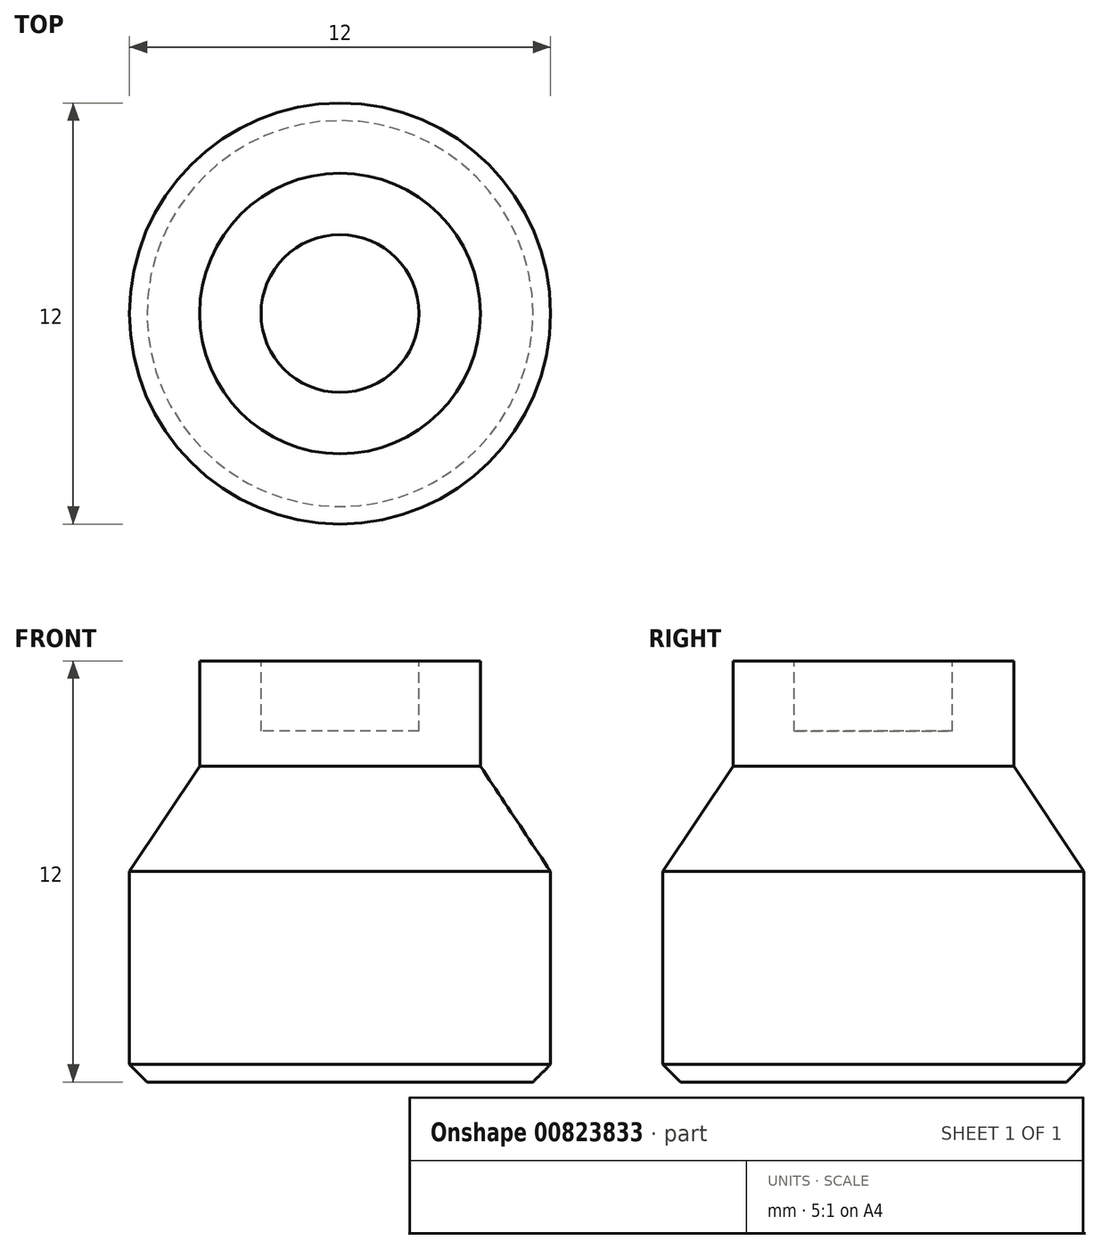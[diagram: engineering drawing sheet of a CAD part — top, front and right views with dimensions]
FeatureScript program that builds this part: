
annotation { "Feature Type Name" : "Feature", "Feature Type Description" : "" }
export const myFeature = defineFeature(function(context is Context, id is Id, definition is map)
    precondition{}
    {
        {
            var Q0;
            Q0=qCreatedBy(makeId("Front.planeOp"),FACE);
            var sketch = newSketch(context, id + "F0", { "sketchPlane" : qUnion([Q0])});
            skLineSegment(sketch, "E0", {"start": v(0, 0) * mm, "end": v(6, 0) * mm});
            skLineSegment(sketch, "E1", {"start": v(6, 0) * mm, "end": v(6, 6) * mm});
            skLineSegment(sketch, "E2", {"start": v(6, 6) * mm, "end": v(4, 9) * mm});
            skLineSegment(sketch, "E3", {"start": v(4, 9) * mm, "end": v(4, 12) * mm});
            skLineSegment(sketch, "E4", {"start": v(4, 12) * mm, "end": v(0, 12) * mm});
            skLineSegment(sketch, "E5", {"start": v(0, 12) * mm, "end": v(0, 0) * mm});
            skSolve(sketch);
        }
        {
            var Q0;
            Q0=makeQuery(id+"F0.imprint","IMPRINT",FACE,{"disambiguationData":[TD([[makeQuery(id+"F0.imprint","IMPRINT",EDGE,{"derivedFrom":sQuery(id+"F0.wireOp",EDGE,"E0")}),1.0]])]});
            var Q1;
            Q1=sQuery(id+"F0.wireOp",EDGE,"E5");
            revolve(context, id + "F1", {"surfaceOperationType" : NewSurfaceOperationType.NEW, "entities" : qUnion([Q0]), "axis" : qUnion([Q1]), "revolveType" : RevolveType.FULL});
        }
        {
            var Q0;
            Q0=makeQuery(id+"F1.opRevolve","SWEPT_FACE",FACE,{"disambiguationData":[OSD([sQuery(id+"F0.wireOp",EDGE,"E4")])]});
            var sketch = newSketch(context, id + "F2", { "sketchPlane" : qUnion([Q0])});
            skCircle(sketch, "E6", {"center": v(0, 0) * mm, "radius": 2.25 * mm});
            skSolve(sketch);
        }
        {
            var Q0;
            Q0=makeQuery(id+"F2.imprint","IMPRINT",FACE,{"disambiguationData":[TD([[makeQuery(id+"F2.imprint","IMPRINT",EDGE,{"derivedFrom":sQuery(id+"F2.wireOp",EDGE,"E6")}),1.0]])]});
            extrude(context, id + "F3", {"entities" : qUnion([Q0]), "operationType" : NewBodyOperationType.REMOVE, "oppositeDirection" : true, "depth" : 2 * mm, "offsetDistance" : 25 * mm});
        }
        {
            var Q0;
            Q0=makeQuery(id+"F1.opRevolve","SWEPT_EDGE",EDGE,{"disambiguationData":[OSD([sQuery(id+"F0.wireOp",EDGE,"E0"),sQuery(id+"F0.wireOp",EDGE,"E1")])]});
            chamfer(context, id + "F4", {"entities" : qUnion([Q0]), "width" : .5 * mm, "tangentPropagation" : true});
        }
    });
